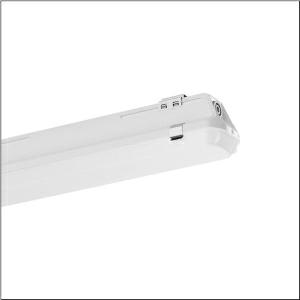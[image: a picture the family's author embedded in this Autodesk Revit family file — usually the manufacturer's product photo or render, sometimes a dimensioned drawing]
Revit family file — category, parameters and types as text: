
# Revit family: monsun_r__11_emergency_51fp10dp460hr_ed92
name_source: partatom
category: Lighting Fixtures
units: mm (PartAtom-declared; Revit-internal decimal feet)

## family parameters
Cut with Voids When Loaded = No
Host = Face
Light Source = No
Part Type = Normal
Room Calculation Point = No
Round Connector Dimension = Use Diameter
Shared = No

## types (1)
- --- (1 x LED, 890 lm, 6.9 W, 4000K)
    Apparent Load = 7 VA
    CIE Flux Codes = 47 77 93 94 100
    Color Rendering = 80
    Color Temperature = 4000K
    Default Elevation = 1800 mm
    Description = Monsun® 11 emergency, damp-proof luminaire, chain hanger, primary optical cover: enclosure, of PMMA, light emission: direct distribution, primary light characteristic: symmetric, installation type: suspended mounting, surface-mounted, horizontal mounting, vertical mounting, LED, rated luminous flux: 6.050lm, luminous efficacy: 175lm/W, light colour: 840, colour temperature: 4000K, control gear: ECG DALI, with terminal, 5+2-pole, max. 2.5mm², mains connection: 220..240V, AC/DC, 0/50..60Hz, rated input power: 35W, changeover relay for equivalent power supply, AC/DC, 0/50..60Hz, luminaire housing, of glass-fibre reinforced polyester, uncoated, bright grey, incl. chain hanger, length: 1.590mm, width: 90mm, height: 88mm, clip for enclosure, of stainless steel (V2A), ceiling mounting element, of stainless steel (V2A), chain hanger, of stainless steel (V2A), protection rating (complete): IP66, insulation class (complete): insulation class I (protective earthing), certification: CE, UKCA, protection symbol: D, impact resistance: IK04, permissible operating ambient temperature: -25..+35°C, standard: EN 50419, EN 60598-2-1, EN 60598-2-22, no direct snow, no direct sun, no direct rain, for indoor or canopied outdoor use, corresponds to IFS (International Featured Standards) requirements for safety and quality in the food industry, contact your sales advisor before using the luminaires in applications with unclear chemical exposure, large temperature fluctuations or condensation-forming humidity, LABS conformity tested according to VDMA 24364:2018-05, packaging unit: 1 piece
    Height = 89 mm
    Lamp = 1 x LED
    Lamp Light Flux = 890 lm
    Lamp Power = 6.9 W
    Lamp count = 1
    Length = 1590 mm
    Luminous efficacy = 129 lm/W
    Manufacturer = Siteco
    ModVariant = No
    Model = 51FP10DP460HR
    Mounting Place = Ceiling
    Mounting Type = Surface mounted
    Number of Poles = 1
    OnlyDefault = Yes
    Power Factor = 1
    Product Name = Monsun® 11 emergency
    Product group = damp-proof luminaire
    ProductGroupID = 300
    Protection Class = Protection class I
    Protection Degree = IP 66
    RLX_Detail_Level = 1
    RLX_Emergency_Light_Flux = 0 lm
    RLX_Emergency_Type = 0
    RLX_Emergency_Type_DB = No
    RlxData = <blob elided: 92269 chars, md5=59473355>
    Socket = socket
    Standby Power = 0 W
    System Light Flux = 890 lm
    System Power = 7 W
    Type Comments = : equivalent power supply (DC)
    Type Image = l_1319650.jpg
    URL = http://relux.com
    VarID = @adj_171461
    Voltage = 0 V
    Weight = 0.00 kg
    Width = 90 mm

## geometry (parser evidence)
native form markers: Blend x4, Sweep x13
no freeform markers — native parametric forms only
